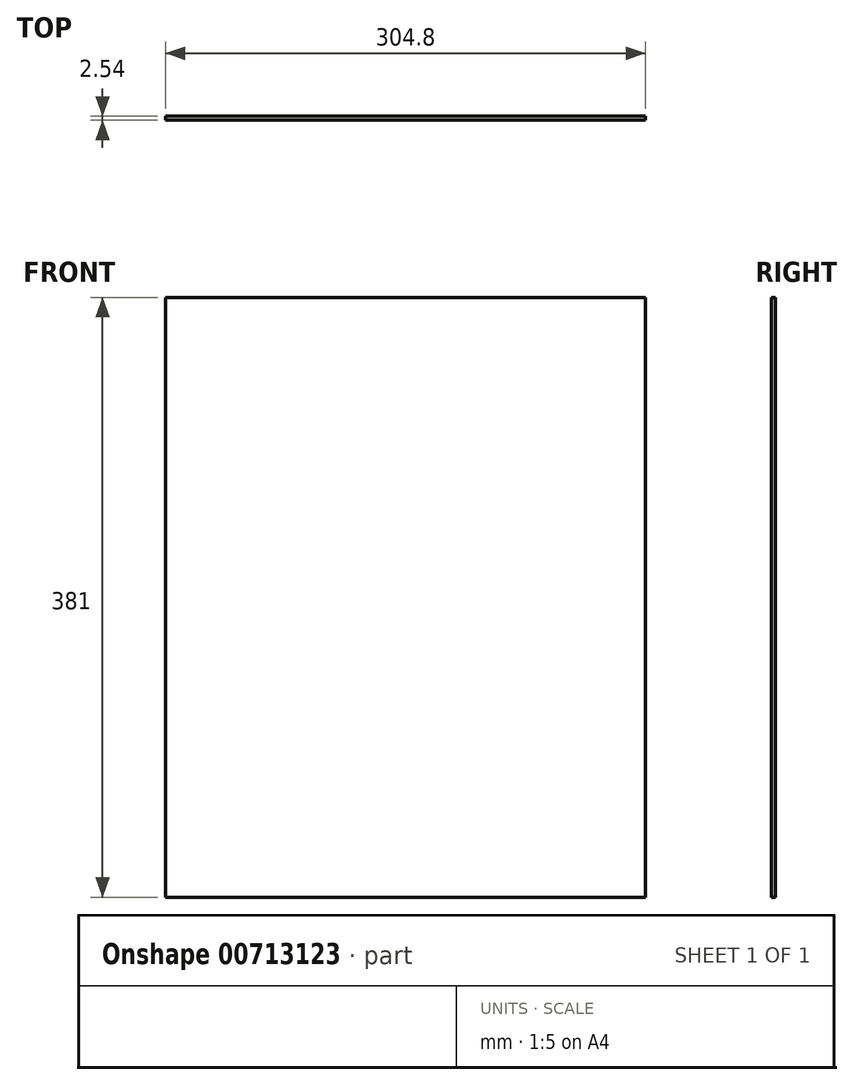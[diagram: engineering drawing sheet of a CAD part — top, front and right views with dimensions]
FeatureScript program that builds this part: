
annotation { "Feature Type Name" : "Feature", "Feature Type Description" : "" }
export const myFeature = defineFeature(function(context is Context, id is Id, definition is map)
    precondition{}
    {
        {
            var Q0;
            Q0=qCreatedBy(makeId("Front.planeOp"),FACE);
            var sketch = newSketch(context, id + "F0", { "sketchPlane" : qUnion([Q0])});
            skLineSegment(sketch, "E0.bottom", {"start": v(-152.4, 190.5) * mm, "end": v(152.4, 190.5) * mm});
            skLineSegment(sketch, "E0.top", {"start": v(-152.4, -190.5) * mm, "end": v(152.4, -190.5) * mm});
            skLineSegment(sketch, "E0.left", {"start": v(-152.4, 190.5) * mm, "end": v(-152.4, -190.5) * mm});
            skLineSegment(sketch, "E0.right", {"start": v(152.4, 190.5) * mm, "end": v(152.4, -190.5) * mm});
            skPoint(sketch, "E0.middle", {"position": v(0, 0) * mm});
            skSolve(sketch);
        }
        {
            var Q0;
            Q0=makeQuery(id+"F0.imprint","IMPRINT",FACE,{"disambiguationData":[TD([[makeQuery(id+"F0.imprint","IMPRINT",EDGE,{"derivedFrom":sQuery(id+"F0.wireOp",EDGE,"E0.bottom")}),-1.0]])]});
            extrude(context, id + "F1", {"entities" : qUnion([Q0]), "depth" : 2.54 * mm, "offsetDistance" : 25.4 * mm});
        }
    });
